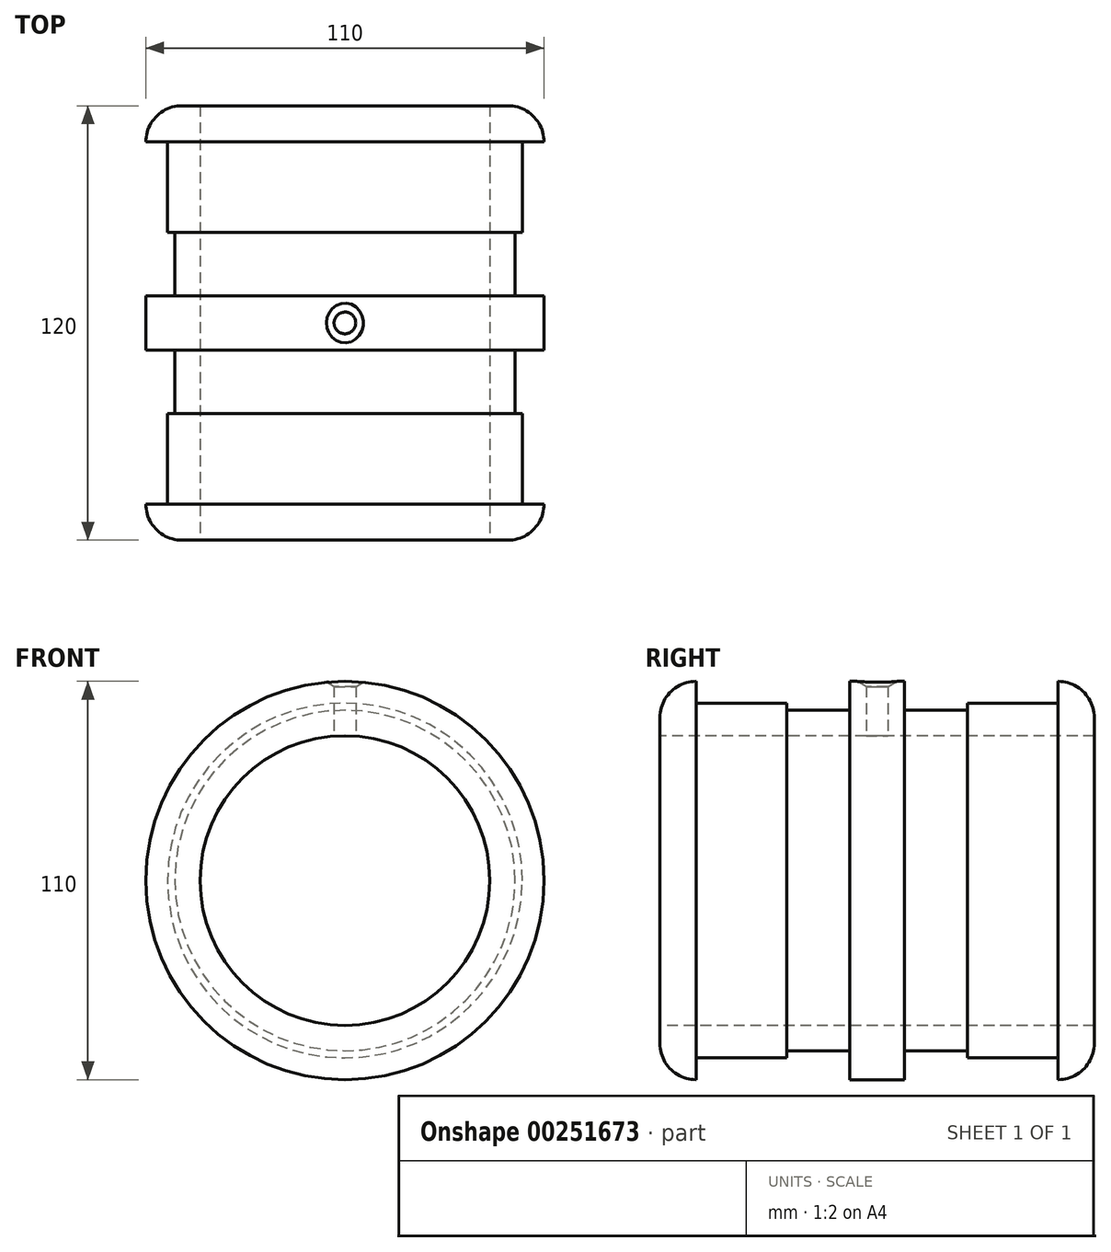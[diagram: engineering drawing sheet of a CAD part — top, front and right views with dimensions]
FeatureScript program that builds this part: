
annotation { "Feature Type Name" : "Feature", "Feature Type Description" : "" }
export const myFeature = defineFeature(function(context is Context, id is Id, definition is map)
    precondition{}
    {
        {
            var Q0;
            Q0=qCreatedBy(makeId("Right.planeOp"),FACE);
            var sketch = newSketch(context, id + "F0", { "sketchPlane" : qUnion([Q0])});
            skLineSegment(sketch, "E0", {"start": v(-86.72, 0) * mm, "end": v(71.3, 0) * mm, "construction": true});
            skLineSegment(sketch, "E1", {"start": v(-60, 40) * mm, "end": v(-60, 55) * mm});
            skLineSegment(sketch, "E2", {"start": v(-60, 55) * mm, "end": v(-50, 55) * mm});
            skLineSegment(sketch, "E3", {"start": v(-50, 55) * mm, "end": v(-50, 49) * mm});
            skLineSegment(sketch, "E4", {"start": v(-50, 49) * mm, "end": v(-25, 49) * mm});
            skLineSegment(sketch, "E5", {"start": v(-25, 49) * mm, "end": v(-25, 47) * mm});
            skLineSegment(sketch, "E6", {"start": v(-25, 47) * mm, "end": v(-7.5, 47) * mm});
            skLineSegment(sketch, "E7", {"start": v(-7.5, 47) * mm, "end": v(-7.5, 55) * mm});
            skLineSegment(sketch, "E8", {"start": v(-7.5, 55) * mm, "end": v(7.5, 55) * mm});
            skLineSegment(sketch, "E9", {"start": v(7.5, 55) * mm, "end": v(7.5, 47) * mm});
            skLineSegment(sketch, "E10", {"start": v(7.5, 47) * mm, "end": v(25, 47) * mm});
            skLineSegment(sketch, "E11", {"start": v(25, 47) * mm, "end": v(25, 49) * mm});
            skLineSegment(sketch, "E12", {"start": v(25, 49) * mm, "end": v(50, 49) * mm});
            skLineSegment(sketch, "E13", {"start": v(50, 49) * mm, "end": v(50, 55) * mm});
            skLineSegment(sketch, "E14", {"start": v(50, 55) * mm, "end": v(60, 55) * mm});
            skLineSegment(sketch, "E15", {"start": v(60, 55) * mm, "end": v(60, 40) * mm});
            skLineSegment(sketch, "E16", {"start": v(60, 40) * mm, "end": v(-60, 40) * mm});
            skSolve(sketch);
        }
        {
            var Q0;
            Q0=makeQuery(id+"F0.imprint","IMPRINT",FACE,{"disambiguationData":[TD([[makeQuery(id+"F0.imprint","IMPRINT",EDGE,{"derivedFrom":sQuery(id+"F0.wireOp",EDGE,"E1")}),-1.0]])]});
            var Q1;
            Q1=sQuery(id+"F0.wireOp",EDGE,"E0");
            revolve(context, id + "F1", {"entities" : qUnion([Q0]), "axis" : qUnion([Q1]), "revolveType" : RevolveType.FULL});
        }
        {
            var Q0;
            Q0=qCreatedBy(makeId("Right.planeOp"),FACE);
            var sketch = newSketch(context, id + "F2", { "sketchPlane" : qUnion([Q0])});
            skLineSegment(sketch, "E17", {"start": v(0, 67.09) * mm, "end": v(0, 33.02) * mm, "construction": true});
            skLineSegment(sketch, "E18", {"start": v(0, 56) * mm, "end": v(7.23, 56) * mm});
            skLineSegment(sketch, "E19", {"start": v(7.23, 56) * mm, "end": v(3, 53.56) * mm});
            skLineSegment(sketch, "E20", {"start": v(3, 53.56) * mm, "end": v(3, 36) * mm});
            skLineSegment(sketch, "E21", {"start": v(3, 36) * mm, "end": v(0, 36) * mm});
            skLineSegment(sketch, "E22", {"start": v(0, 36) * mm, "end": v(0, 56) * mm});
            skPoint(sketch, "E23", {"position": v(3, 40) * mm});
            skPoint(sketch, "E24", {"position": v(5.5, 55) * mm});
            skSolve(sketch);
        }
        {
            var Q0;
            Q0=makeQuery(id+"F2.imprint","IMPRINT",FACE,{"disambiguationData":[TD([[makeQuery(id+"F2.imprint","IMPRINT",EDGE,{"derivedFrom":sQuery(id+"F2.wireOp",EDGE,"E18")}),-1.0]])]});
            var Q1;
            Q1=sQuery(id+"F2.wireOp",EDGE,"E17");
            revolve(context, id + "F3", {"operationType" : NewBodyOperationType.REMOVE, "entities" : qUnion([Q0]), "axis" : qUnion([Q1]), "revolveType" : RevolveType.FULL, "oppositeDirection" : true});
        }
        {
            var Q0;
            Q0=makeQuery(id+"F1.opRevolve","SWEPT_EDGE",EDGE,{"disambiguationData":[OSD([sQuery(id+"F0.wireOp",EDGE,"E14"),sQuery(id+"F0.wireOp",EDGE,"E15")])]});
            var Q1;
            Q1=makeQuery(id+"F1.opRevolve","SWEPT_EDGE",EDGE,{"disambiguationData":[OSD([sQuery(id+"F0.wireOp",EDGE,"E1"),sQuery(id+"F0.wireOp",EDGE,"E2")])]});
            fillet(context, id + "F4", {"entities" : qUnion([Q0, Q1]), "radius" : 10 * mm, "tangentPropagation" : true, "allowEdgeOverflow" : false});
        }
    });
